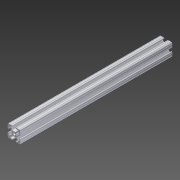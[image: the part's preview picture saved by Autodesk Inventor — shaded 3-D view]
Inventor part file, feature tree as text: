
AUTODESK INVENTOR PART (.ipt)
format: ipt  version: 2013 (Build 170138000, 138)  size: 163,328 bytes
history: native  units: in
note: dims shown in document units (in); Inventor stores cm internally (conversion verified against a paired STEP export)
features: extrude x1, imported_body x1
ambient origin geometry x8: Origin, YZ Plane, XZ Plane, XY Plane, X Axis, Y Axis, Z Axis, Center Point
feature tree (2):
  extrude  "Extrude1"  [1 undecoded]
  imported_body  "Base1"
note: 1 required parameter value undecoded (feature->parameter linkage not recoverable at this tier; creation-order binding heuristic only, values carry confidence <= 0.55)
